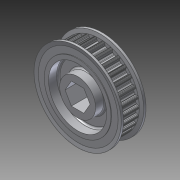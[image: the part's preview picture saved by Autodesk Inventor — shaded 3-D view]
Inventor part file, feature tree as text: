
AUTODESK INVENTOR PART (.ipt)
format: ipt  version: 2014 SP1 (Build 180222100, 222)  size: 1,317,376 bytes
history: native  units: in
note: dims shown in document units (in); Inventor stores cm internally (conversion verified against a paired STEP export)
features: mirror x1, other x1, imported_body x1
ambient origin geometry x8: Origin, YZ Plane, XZ Plane, XY Plane, X Axis, Y Axis, Z Axis, Center Point
bodies: Body1 (feature_tree)
feature tree (3):
  mirror  "Mirror1"
  other  "217-3229-STEP1"
  imported_body  "Base1"
